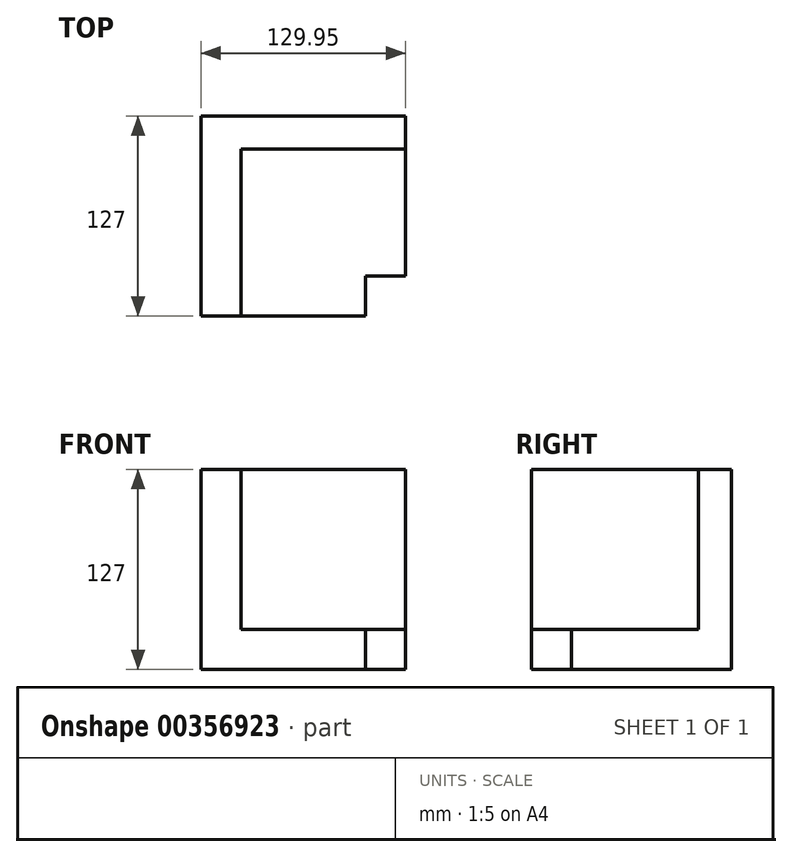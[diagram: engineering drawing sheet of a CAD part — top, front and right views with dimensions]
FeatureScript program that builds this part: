
annotation { "Feature Type Name" : "Feature", "Feature Type Description" : "" }
export const myFeature = defineFeature(function(context is Context, id is Id, definition is map)
    precondition{}
    {
        {
            var Q0;
            Q0=qCreatedBy(makeId("Top.planeOp"),FACE);
            var sketch = newSketch(context, id + "F0", { "sketchPlane" : qUnion([Q0])});
            skLineSegment(sketch, "E0.bottom", {"start": v(-57.27, -60.62) * mm, "end": v(72.68, -60.62) * mm});
            skLineSegment(sketch, "E0.top", {"start": v(-57.27, 66.38) * mm, "end": v(72.68, 66.38) * mm});
            skLineSegment(sketch, "E0.left", {"start": v(-57.27, -60.62) * mm, "end": v(-57.27, 66.38) * mm});
            skLineSegment(sketch, "E0.right", {"start": v(72.68, -60.62) * mm, "end": v(72.68, 66.38) * mm});
            skSolve(sketch);
        }
        {
            var Q0;
            Q0=makeQuery(id+"F0.imprint","IMPRINT",FACE,{"disambiguationData":[TD([[makeQuery(id+"F0.imprint","IMPRINT",EDGE,{"derivedFrom":sQuery(id+"F0.wireOp",EDGE,"E0.bottom")}),1.0]])]});
            extrude(context, id + "F1", {"entities" : qUnion([Q0]), "depth" : 25.4 * mm});
        }
        {
            var Q0;
            Q0=makeQuery(id+"F1.opExtrude","CAP_FACE",FACE,{"disambiguationData":[OSD([sQuery(id+"F0.wireOp",EDGE,"E0.bottom"),sQuery(id+"F0.wireOp",EDGE,"E0.top"),sQuery(id+"F0.wireOp",EDGE,"E0.left"),sQuery(id+"F0.wireOp",EDGE,"E0.right")])],"isStart":false});
            var sketch = newSketch(context, id + "F2", { "sketchPlane" : qUnion([Q0])});
            skLineSegment(sketch, "E1.bottom", {"start": v(-57.27, -60.62) * mm, "end": v(-31.87, -60.62) * mm});
            skLineSegment(sketch, "E1.top", {"start": v(-57.27, 66.38) * mm, "end": v(-31.87, 66.38) * mm});
            skLineSegment(sketch, "E1.left", {"start": v(-57.27, -60.62) * mm, "end": v(-57.27, 66.38) * mm});
            skLineSegment(sketch, "E1.right", {"start": v(-31.87, -60.62) * mm, "end": v(-31.87, 66.38) * mm});
            skSolve(sketch);
        }
        {
            var Q0;
            Q0=makeQuery(id+"F2.imprint","IMPRINT",FACE,{"disambiguationData":[TD([[makeQuery(id+"F2.imprint","IMPRINT",EDGE,{"derivedFrom":sQuery(id+"F2.wireOp",EDGE,"E1.bottom")}),1.0]])]});
            extrude(context, id + "F3", {"entities" : qUnion([Q0]), "operationType" : NewBodyOperationType.ADD, "depth" : 25.4 * mm});
        }
        {
            var Q0;
            Q0=makeQuery(id+"F3.opExtrude","CAP_FACE",FACE,{"disambiguationData":[OSD([sQuery(id+"F2.wireOp",EDGE,"E1.bottom"),sQuery(id+"F2.wireOp",EDGE,"E1.top"),sQuery(id+"F2.wireOp",EDGE,"E1.left"),sQuery(id+"F2.wireOp",EDGE,"E1.right")])],"isStart":false});
            extrude(context, id + "F4", {"entities" : qUnion([Q0]), "operationType" : NewBodyOperationType.ADD, "depth" : 76.2 * mm});
        }
        {
            var Q0;
            Q0=makeQuery(id+"F1.opExtrude","CAP_FACE",FACE,{"disambiguationData":[OSD([sQuery(id+"F0.wireOp",EDGE,"E0.bottom"),sQuery(id+"F0.wireOp",EDGE,"E0.top"),sQuery(id+"F0.wireOp",EDGE,"E0.left"),sQuery(id+"F0.wireOp",EDGE,"E0.right")])],"isStart":false});
            var sketch = newSketch(context, id + "F5", { "sketchPlane" : qUnion([Q0])});
            skLineSegment(sketch, "E2.bottom", {"start": v(72.68, 66.38) * mm, "end": v(-31.87, 66.38) * mm});
            skLineSegment(sketch, "E2.top", {"start": v(72.68, 45.34) * mm, "end": v(-31.87, 45.34) * mm});
            skLineSegment(sketch, "E2.left", {"start": v(72.68, 66.38) * mm, "end": v(72.68, 45.34) * mm});
            skLineSegment(sketch, "E2.right", {"start": v(-31.87, 66.38) * mm, "end": v(-31.87, 45.34) * mm});
            skSolve(sketch);
        }
        {
            var Q0;
            Q0=makeQuery(id+"F5.imprint","IMPRINT",FACE,{"disambiguationData":[TD([[makeQuery(id+"F5.imprint","IMPRINT",EDGE,{"derivedFrom":sQuery(id+"F5.wireOp",EDGE,"E2.bottom")}),-1.0]])]});
            extrude(context, id + "F6", {"entities" : qUnion([Q0]), "operationType" : NewBodyOperationType.ADD, "depth" : 101.6 * mm});
        }
        {
            var Q0;
            Q0=makeQuery(id+"F1.opExtrude","CAP_FACE",FACE,{"disambiguationData":[OSD([sQuery(id+"F0.wireOp",EDGE,"E0.bottom"),sQuery(id+"F0.wireOp",EDGE,"E0.top"),sQuery(id+"F0.wireOp",EDGE,"E0.left"),sQuery(id+"F0.wireOp",EDGE,"E0.right")])],"isStart":false});
            var sketch = newSketch(context, id + "F7", { "sketchPlane" : qUnion([Q0])});
            skLineSegment(sketch, "E3.bottom", {"start": v(72.68, -60.62) * mm, "end": v(47.28, -60.62) * mm});
            skLineSegment(sketch, "E3.top", {"start": v(72.68, -35.22) * mm, "end": v(47.28, -35.22) * mm});
            skLineSegment(sketch, "E3.left", {"start": v(72.68, -60.62) * mm, "end": v(72.68, -35.22) * mm});
            skLineSegment(sketch, "E3.right", {"start": v(47.28, -60.62) * mm, "end": v(47.28, -35.22) * mm});
            skSolve(sketch);
        }
        {
            var Q0;
            Q0=makeQuery(id+"F7.imprint","IMPRINT",FACE,{"disambiguationData":[TD([[makeQuery(id+"F7.imprint","IMPRINT",EDGE,{"derivedFrom":sQuery(id+"F7.wireOp",EDGE,"E3.bottom")}),1.0]])]});
            extrude(context, id + "F8", {"entities" : qUnion([Q0]), "operationType" : NewBodyOperationType.REMOVE, "oppositeDirection" : true, "depth" : 25.4 * mm});
        }
    });
